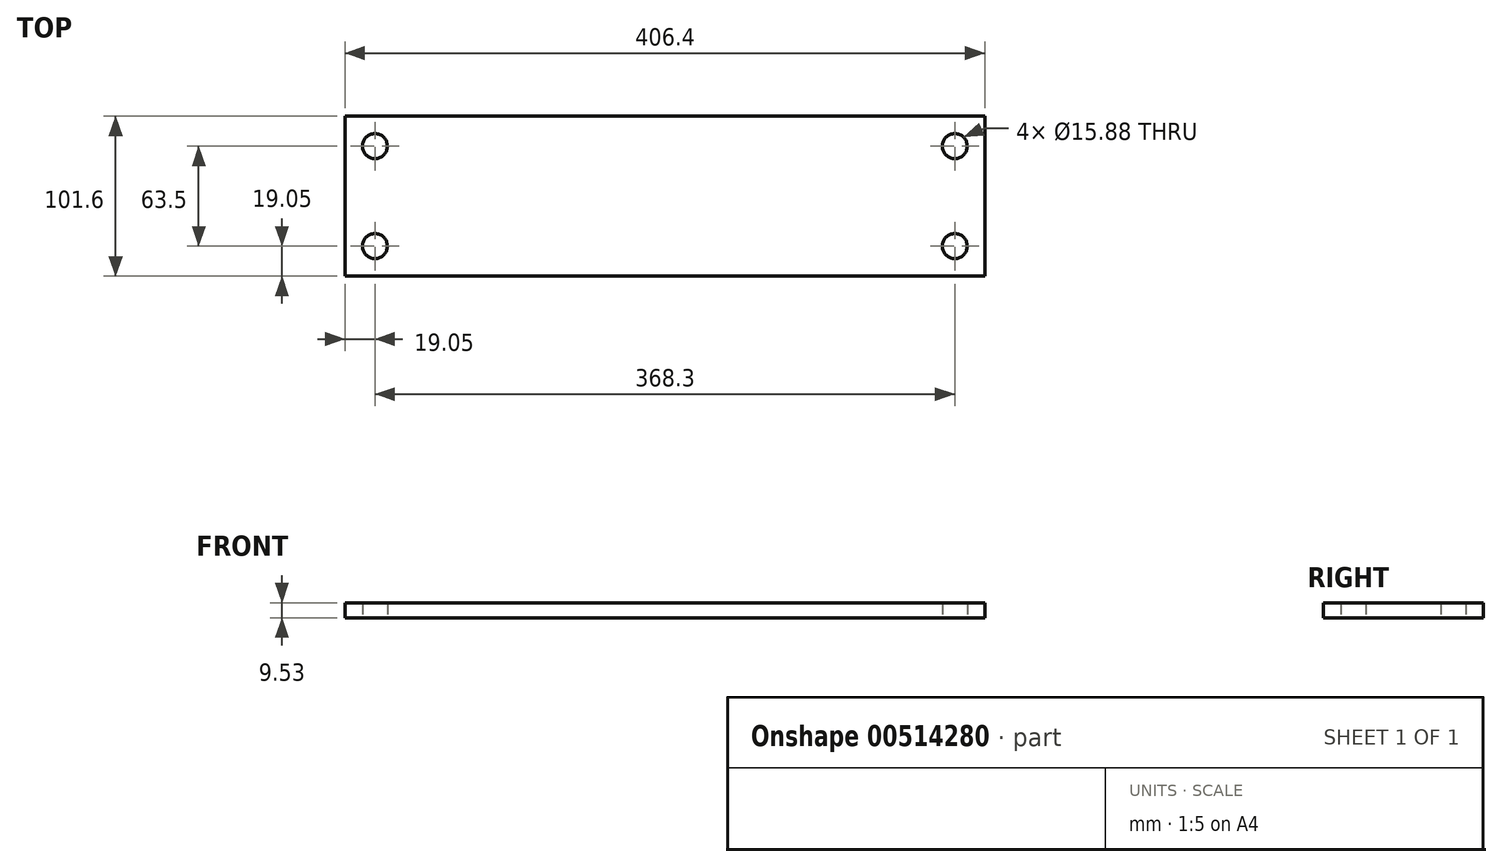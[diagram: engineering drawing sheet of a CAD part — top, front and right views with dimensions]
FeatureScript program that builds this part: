
annotation { "Feature Type Name" : "Feature", "Feature Type Description" : "" }
export const myFeature = defineFeature(function(context is Context, id is Id, definition is map)
    precondition{}
    {
        {
            var Q0;
            Q0=qCreatedBy(makeId("Top.planeOp"),FACE);
            var sketch = newSketch(context, id + "F0", { "sketchPlane" : qUnion([Q0])});
            skLineSegment(sketch, "E0.bottom", {"start": v(203.2, -50.8) * mm, "end": v(-203.2, -50.8) * mm});
            skLineSegment(sketch, "E0.top", {"start": v(203.2, 50.8) * mm, "end": v(-203.2, 50.8) * mm});
            skLineSegment(sketch, "E0.left", {"start": v(203.2, -50.8) * mm, "end": v(203.2, 50.8) * mm});
            skLineSegment(sketch, "E0.right", {"start": v(-203.2, -50.8) * mm, "end": v(-203.2, 50.8) * mm});
            skPoint(sketch, "E0.middle", {"position": v(0, 0) * mm});
            skCircle(sketch, "E1", {"center": v(-184.15, 31.75) * mm, "radius": 7.94 * mm});
            skCircle(sketch, "E2.MirrorC", {"center": v(184.15, 31.75) * mm, "radius": 7.94 * mm});
            skCircle(sketch, "E3.MirrorC", {"center": v(184.15, -31.75) * mm, "radius": 7.94 * mm});
            skCircle(sketch, "E4.MirrorC", {"center": v(-184.15, -31.75) * mm, "radius": 7.94 * mm});
            skSolve(sketch);
        }
        {
            var Q0;
            Q0 = qSketchRegion(id + "F0", true);
            extrude(context, id + "F1", {"entities" : qUnion([Q0]), "depth" : 9.52 * mm});
        }
    });
